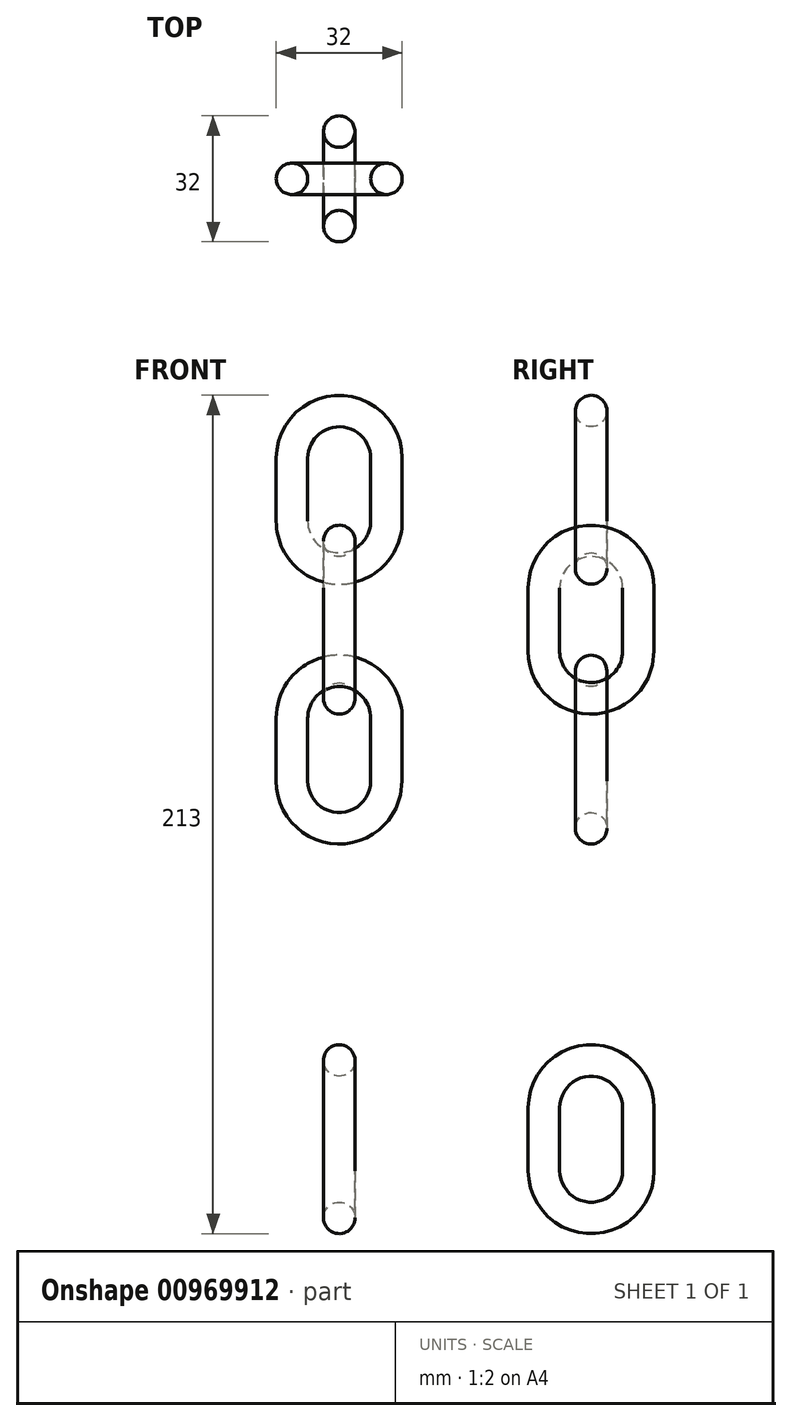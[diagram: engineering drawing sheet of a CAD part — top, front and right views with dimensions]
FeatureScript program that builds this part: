
annotation { "Feature Type Name" : "Feature", "Feature Type Description" : "" }
export const myFeature = defineFeature(function(context is Context, id is Id, definition is map)
    precondition{}
    {
        {
            var Q0;
            Q0=qCreatedBy(makeId("Top.planeOp"),FACE);
            var sketch = newSketch(context, id + "F0", { "sketchPlane" : qUnion([Q0])});
            skCircle(sketch, "E0", {"center": v(0, 12) * mm, "radius": 4 * mm});
            skSolve(sketch);
        }
        {
            var Q0;
            Q0=qCreatedBy(makeId("Right.planeOp"),FACE);
            var sketch = newSketch(context, id + "F1", { "sketchPlane" : qUnion([Q0])});
            skLineSegment(sketch, "E1.bottom", {"start": v(-12, -8) * mm, "end": v(12, -8) * mm, "construction": true});
            skLineSegment(sketch, "E1.top", {"start": v(-12, 8) * mm, "end": v(12, 8) * mm, "construction": true});
            skLineSegment(sketch, "E1.left", {"start": v(-12, -8) * mm, "end": v(-12, 8) * mm});
            skLineSegment(sketch, "E1.right", {"start": v(12, -8) * mm, "end": v(12, 8) * mm});
            skLineSegment(sketch, "E2", {"start": v(-12, -8) * mm, "end": v(0, 0) * mm, "construction": true});
            skLineSegment(sketch, "E3", {"start": v(0, 0) * mm, "end": v(12, -8) * mm, "construction": true});
            skArc(sketch, "E4", {"start": v(-12, -8) * mm, "mid": v(0, -20) * mm, "end": v(12, -8) * mm});
            skLineSegment(sketch, "E5", {"start": v(0, 0) * mm, "end": v(-12, 0) * mm, "construction": true});
            skArc(sketch, "E6.MirrorCS", {"start": v(-12, 8) * mm, "mid": v(0, 20) * mm, "end": v(12, 8) * mm});
            skSolve(sketch);
        }
        {
            var Q0;
            Q0=makeQuery(id+"F0.imprint","IMPRINT",FACE,{"disambiguationData":[TD([[makeQuery(id+"F0.imprint","IMPRINT",EDGE,{"derivedFrom":sQuery(id+"F0.wireOp",EDGE,"E0")}),1.0]])]});
            var Q1;
            Q1=sQuery(id+"F1.wireOp",EDGE,"E1.right");
            var Q2;
            Q2=sQuery(id+"F1.wireOp",EDGE,"E4");
            var Q3;
            Q3=sQuery(id+"F1.wireOp",EDGE,"E1.left");
            var Q4;
            Q4=sQuery(id+"F1.wireOp",EDGE,"E6.MirrorCS");
            sweep(context, id + "F2", {"profiles" : qUnion([Q0]), "path" : qUnion([Q1, Q2, Q3, Q4])});
        }
        {
            var Q0;
            Q0=makeQuery(id+"F2.opSweep","SWEPT_BODY",BODY,{"disambiguationData":[OSD([sQuery(id+"F0.wireOp",EDGE,"E0"),sQuery(id+"F1.wireOp",EDGE,"E4")])]});
            transform(context, id + "F3", {"entities" : qUnion([Q0]), "transformType" : TransformType.TRANSLATION_3D, "dx" : 0 * mm, "dy" : 0 * mm, "dz" : 33 * mm, "makeCopy" : true});
        }
        {
            var Q0;
            Q0=qCreatedBy(makeId("Right.planeOp"),FACE);
            var sketch = newSketch(context, id + "F4", { "sketchPlane" : qUnion([Q0])});
            skLineSegment(sketch, "E7", {"start": v(0, 0) * mm, "end": v(0, 71.54) * mm, "construction": true});
            skSolve(sketch);
        }
        {
            var Q0;
            Q0=makeQuery(id+"F3.opPattern","COPY",BODY,{"derivedFrom":makeQuery(id+"F2.opSweep","SWEPT_BODY",BODY,{"disambiguationData":[OSD([sQuery(id+"F0.wireOp",EDGE,"E0"),sQuery(id+"F1.wireOp",EDGE,"E4")])]}),"instanceName":"1"});
            var Q1;
            Q1=sQuery(id+"F4.wireOp",EDGE,"E7");
            transform(context, id + "F5", {"entities" : qUnion([Q0]), "transformType" : TransformType.ROTATION, "transformAxis" : qUnion([Q1]), "angle" : 90 * degree, "makeCopy" : false});
        }
        {
            var Q0;
            Q0=makeQuery(id+"F3.opPattern","COPY",BODY,{"derivedFrom":makeQuery(id+"F2.opSweep","SWEPT_BODY",BODY,{"disambiguationData":[OSD([sQuery(id+"F0.wireOp",EDGE,"E0"),sQuery(id+"F1.wireOp",EDGE,"E4")])]}),"instanceName":"1"});
            transform(context, id + "F6", {"entities" : qUnion([Q0]), "transformType" : TransformType.TRANSLATION_3D, "dx" : 0 * mm, "dy" : 0 * mm, "dz" : 66 * mm, "makeCopy" : true});
        }
        {
            var Q0;
            Q0=makeQuery(id+"F3.opPattern","COPY",BODY,{"derivedFrom":makeQuery(id+"F2.opSweep","SWEPT_BODY",BODY,{"disambiguationData":[OSD([sQuery(id+"F0.wireOp",EDGE,"E0"),sQuery(id+"F1.wireOp",EDGE,"E4")])]}),"instanceName":"1"});
            transform(context, id + "F7", {"entities" : qUnion([Q0]), "transformType" : TransformType.TRANSLATION_3D, "dx" : 0 * mm, "dy" : 0 * mm, "dz" : 132 * mm, "makeCopy" : true});
        }
        {
            var Q0;
            Q0=makeQuery(id+"F3.opPattern","COPY",BODY,{"derivedFrom":makeQuery(id+"F2.opSweep","SWEPT_BODY",BODY,{"disambiguationData":[OSD([sQuery(id+"F0.wireOp",EDGE,"E0"),sQuery(id+"F1.wireOp",EDGE,"E4")])]}),"instanceName":"1"});
            transform(context, id + "F8", {"entities" : qUnion([Q0]), "transformType" : TransformType.TRANSLATION_3D, "dx" : 0 * mm, "dy" : 0 * mm, "dz" : 66 * mm, "makeCopy" : true});
        }
        {
            var Q0;
            Q0=makeQuery(id+"F3.opPattern","COPY",BODY,{"derivedFrom":makeQuery(id+"F2.opSweep","SWEPT_BODY",BODY,{"disambiguationData":[OSD([sQuery(id+"F0.wireOp",EDGE,"E0"),sQuery(id+"F1.wireOp",EDGE,"E4")])]}),"instanceName":"1"});
            var Q1;
            Q1=makeQuery(id+"F8.opPattern","COPY",BODY,{"derivedFrom":makeQuery(id+"F3.opPattern","COPY",BODY,{"derivedFrom":makeQuery(id+"F2.opSweep","SWEPT_BODY",BODY,{"disambiguationData":[OSD([sQuery(id+"F0.wireOp",EDGE,"E0"),sQuery(id+"F1.wireOp",EDGE,"E4")])]}),"instanceName":"1"}),"instanceName":"1"});
            booleanBodies(context, id + "F9", {"operationType" : BooleanOperationType.SUBTRACTION, "tools" : qUnion([Q0]), "targets" : qUnion([Q1]), "keepTools" : true});
        }
        {
            var Q0;
            Q0=makeQuery(id+"F8.opPattern","COPY",BODY,{"derivedFrom":makeQuery(id+"F3.opPattern","COPY",BODY,{"derivedFrom":makeQuery(id+"F2.opSweep","SWEPT_BODY",BODY,{"disambiguationData":[OSD([sQuery(id+"F0.wireOp",EDGE,"E0"),sQuery(id+"F1.wireOp",EDGE,"E4")])]}),"instanceName":"1"}),"instanceName":"1"});
            transform(context, id + "F10", {"entities" : qUnion([Q0]), "transformType" : TransformType.TRANSLATION_3D, "dx" : 0 * mm, "dy" : 0 * mm, "dz" : 33 * mm, "makeCopy" : true});
        }
        {
            var Q0;
            Q0=makeQuery(id+"F10.opPattern","COPY",BODY,{"derivedFrom":makeQuery(id+"F8.opPattern","COPY",BODY,{"derivedFrom":makeQuery(id+"F3.opPattern","COPY",BODY,{"derivedFrom":makeQuery(id+"F2.opSweep","SWEPT_BODY",BODY,{"disambiguationData":[OSD([sQuery(id+"F0.wireOp",EDGE,"E0"),sQuery(id+"F1.wireOp",EDGE,"E4")])]}),"instanceName":"1"}),"instanceName":"1"}),"instanceName":"1"});
            var Q1;
            Q1=sQuery(id+"F4.wireOp",EDGE,"E7");
            transform(context, id + "F11", {"entities" : qUnion([Q0]), "transformType" : TransformType.ROTATION, "transformAxis" : qUnion([Q1]), "angle" : 90 * degree, "makeCopy" : false});
        }
        {
            var Q0;
            Q0=makeQuery(id+"F3.opPattern","COPY",BODY,{"derivedFrom":makeQuery(id+"F2.opSweep","SWEPT_BODY",BODY,{"disambiguationData":[OSD([sQuery(id+"F0.wireOp",EDGE,"E0"),sQuery(id+"F1.wireOp",EDGE,"E4")])]}),"instanceName":"1"});
            transform(context, id + "F12", {"entities" : qUnion([Q0]), "transformType" : TransformType.TRANSLATION_3D, "dx" : 0 * mm, "dy" : 0 * mm, "dz" : 132 * mm, "makeCopy" : true});
        }
        {
            var Q0;
            Q0=makeQuery(id+"F3.opPattern","COPY",BODY,{"derivedFrom":makeQuery(id+"F2.opSweep","SWEPT_BODY",BODY,{"disambiguationData":[OSD([sQuery(id+"F0.wireOp",EDGE,"E0"),sQuery(id+"F1.wireOp",EDGE,"E4")])]}),"instanceName":"1"});
            var Q1;
            Q1=makeQuery(id+"F12.opPattern","COPY",BODY,{"derivedFrom":makeQuery(id+"F3.opPattern","COPY",BODY,{"derivedFrom":makeQuery(id+"F2.opSweep","SWEPT_BODY",BODY,{"disambiguationData":[OSD([sQuery(id+"F0.wireOp",EDGE,"E0"),sQuery(id+"F1.wireOp",EDGE,"E4")])]}),"instanceName":"1"}),"instanceName":"1"});
            booleanBodies(context, id + "F13", {"operationType" : BooleanOperationType.SUBTRACTION, "tools" : qUnion([Q0]), "targets" : qUnion([Q1])});
        }
    });
